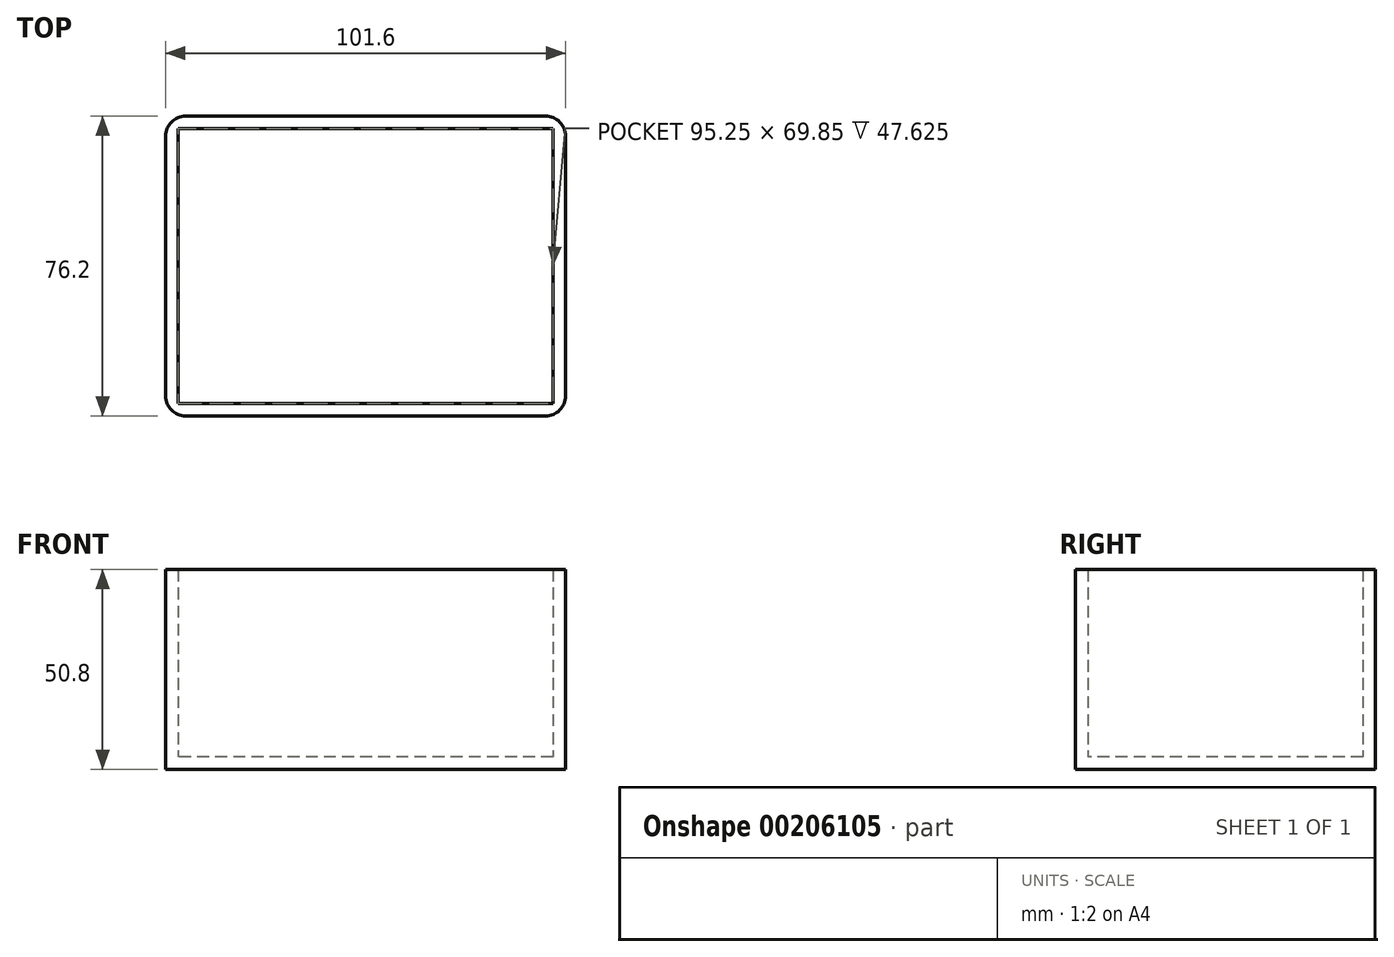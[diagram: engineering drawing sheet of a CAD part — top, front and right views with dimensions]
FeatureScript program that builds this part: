
annotation { "Feature Type Name" : "Feature", "Feature Type Description" : "" }
export const myFeature = defineFeature(function(context is Context, id is Id, definition is map)
    precondition{}
    {
        {
            var Q0;
            Q0=qCreatedBy(makeId("Top.planeOp"),FACE);
            var sketch = newSketch(context, id + "F0", { "sketchPlane" : qUnion([Q0])});
            skLineSegment(sketch, "E0.bottom", {"start": v(50.8, 38.1) * mm, "end": v(-50.8, 38.1) * mm});
            skLineSegment(sketch, "E0.top", {"start": v(50.8, -38.1) * mm, "end": v(-50.8, -38.1) * mm});
            skLineSegment(sketch, "E0.left", {"start": v(50.8, 38.1) * mm, "end": v(50.8, -38.1) * mm});
            skLineSegment(sketch, "E0.right", {"start": v(-50.8, 38.1) * mm, "end": v(-50.8, -38.1) * mm});
            skPoint(sketch, "E0.middle", {"position": v(0, 0) * mm});
            skLineSegment(sketch, "E1.0", {"start": v(47.62, 34.93) * mm, "end": v(-47.63, 34.93) * mm});
            skLineSegment(sketch, "E1.1", {"start": v(47.62, 34.93) * mm, "end": v(47.63, -34.93) * mm});
            skLineSegment(sketch, "E1.2", {"start": v(47.63, -34.93) * mm, "end": v(-47.62, -34.93) * mm});
            skLineSegment(sketch, "E1.3", {"start": v(-47.63, 34.93) * mm, "end": v(-47.62, -34.93) * mm});
            skSolve(sketch);
        }
        {
            var Q0;
            Q0=makeQuery(id+"F0.imprint","IMPRINT",FACE,{"disambiguationData":[TD([[makeQuery(id+"F0.imprint","IMPRINT",EDGE,{"derivedFrom":sQuery(id+"F0.wireOp",EDGE,"E0.bottom")}),1.0]])]});
            extrude(context, id + "F1", {"entities" : qUnion([Q0]), "depth" : 50.8 * mm});
        }
        {
            var Q0;
            Q0=makeQuery(id+"F0.imprint","IMPRINT",FACE,{"disambiguationData":[TD([[makeQuery(id+"F0.imprint","IMPRINT",EDGE,{"derivedFrom":sQuery(id+"F0.wireOp",EDGE,"E1.0")}),1.0]])]});
            extrude(context, id + "F2", {"entities" : qUnion([Q0]), "operationType" : NewBodyOperationType.ADD, "depth" : 3.17 * mm});
        }
        {
            var Q0;
            Q0=makeQuery(id+"F1.opExtrude","SWEPT_EDGE",EDGE,{"disambiguationData":[OSD([sQuery(id+"F0.wireOp",EDGE,"E0.bottom"),sQuery(id+"F0.wireOp",EDGE,"E0.left")])]});
            var Q1;
            Q1=makeQuery(id+"F1.opExtrude","SWEPT_EDGE",EDGE,{"disambiguationData":[OSD([sQuery(id+"F0.wireOp",EDGE,"E0.top"),sQuery(id+"F0.wireOp",EDGE,"E0.left")])]});
            var Q2;
            Q2=makeQuery(id+"F1.opExtrude","SWEPT_EDGE",EDGE,{"disambiguationData":[OSD([sQuery(id+"F0.wireOp",EDGE,"E0.bottom"),sQuery(id+"F0.wireOp",EDGE,"E0.right")])]});
            var Q3;
            Q3=makeQuery(id+"F1.opExtrude","SWEPT_EDGE",EDGE,{"disambiguationData":[OSD([sQuery(id+"F0.wireOp",EDGE,"E0.top"),sQuery(id+"F0.wireOp",EDGE,"E0.right")])]});
            fillet(context, id + "F3", {"entities" : qUnion([Q0, Q1, Q2, Q3]), "radius" : 5.08 * mm, "tangentPropagation" : true, "allowEdgeOverflow" : false});
        }
    });
